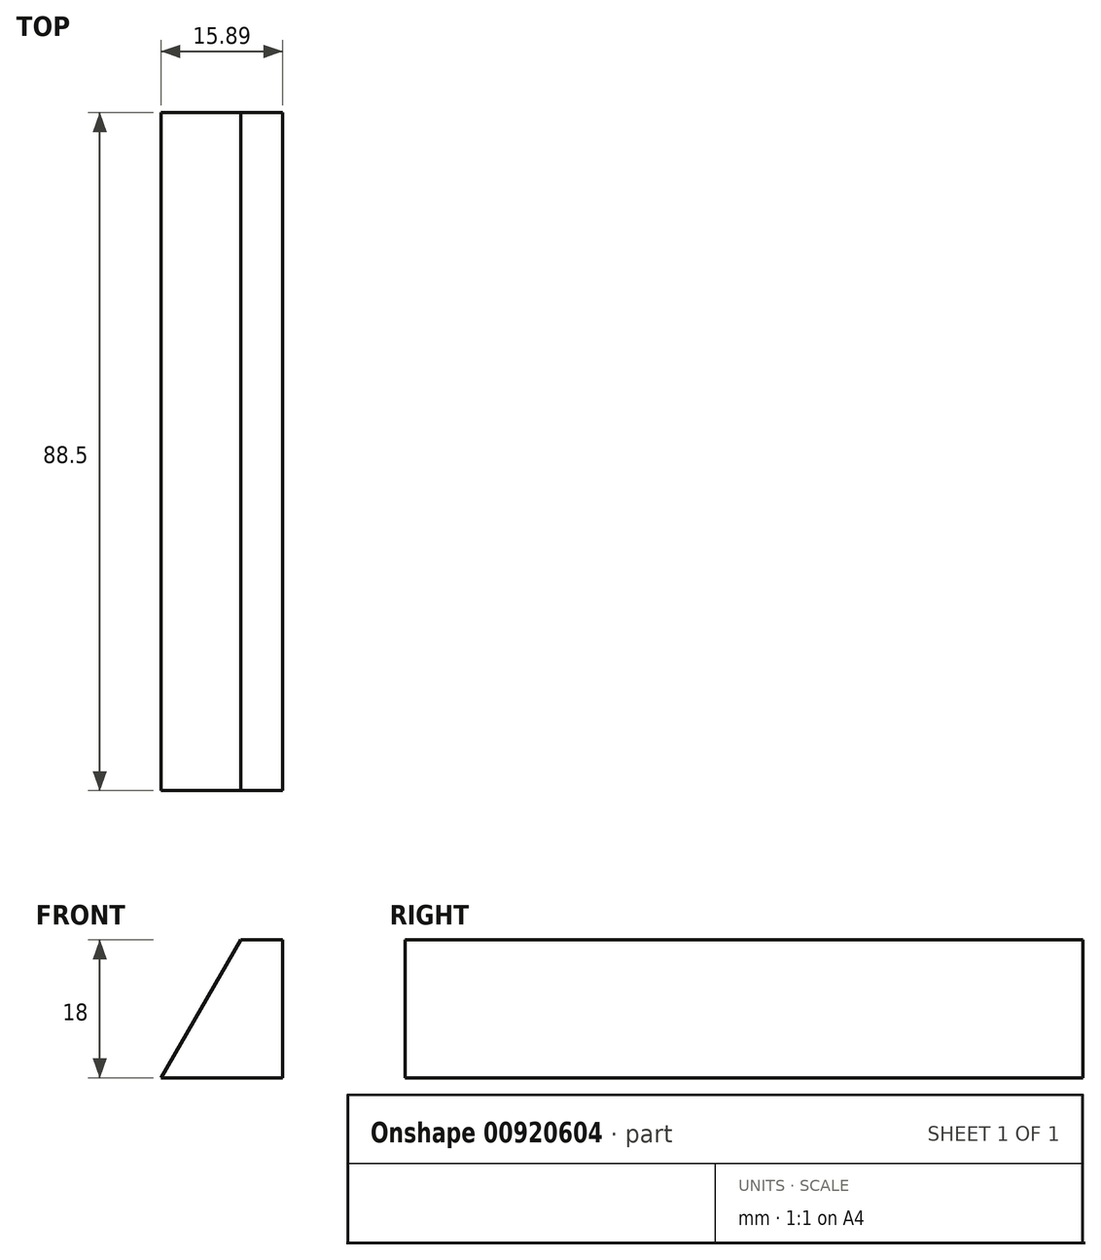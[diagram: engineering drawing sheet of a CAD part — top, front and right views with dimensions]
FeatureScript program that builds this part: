
annotation { "Feature Type Name" : "Feature", "Feature Type Description" : "" }
export const myFeature = defineFeature(function(context is Context, id is Id, definition is map)
    precondition{}
    {
        {
            var Q0;
            Q0=qCreatedBy(makeId("Front.planeOp"),FACE);
            var sketch = newSketch(context, id + "F0", { "sketchPlane" : qUnion([Q0]), "disableImprinting" : false});
            skLineSegment(sketch, "E0", {"start": v(0, 0) * mm, "end": v(-15.9, 0) * mm});
            skLineSegment(sketch, "E1", {"start": v(-15.9, 0) * mm, "end": v(-5.5, 18) * mm});
            skLineSegment(sketch, "E2", {"start": v(-5.5, 18) * mm, "end": v(0, 18) * mm});
            skLineSegment(sketch, "E3", {"start": v(0, 18) * mm, "end": v(0, 0) * mm});
            skSolve(sketch);
        }
        {
            var Q0;
            Q0=makeQuery(id+"F0.imprint","IMPRINT",FACE,{"disambiguationData":[TD([[makeQuery(id+"F0.imprint","IMPRINT",EDGE,{"derivedFrom":sQuery(id+"F0.wireOp",EDGE,"E0")}),-1.0]])]});
            extrude(context, id + "F1", {"entities" : qUnion([Q0]), "depth" : 88.5 * mm, "offsetDistance" : 25 * mm, "symmetric" : true});
        }
    });
